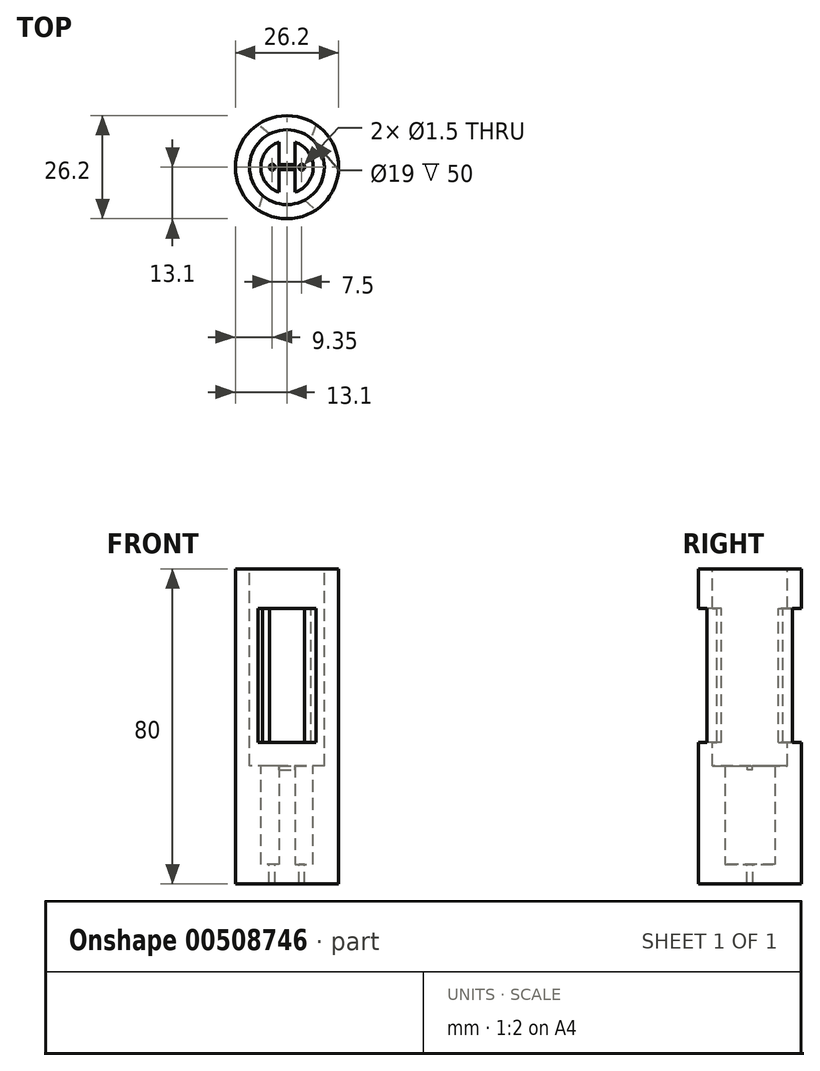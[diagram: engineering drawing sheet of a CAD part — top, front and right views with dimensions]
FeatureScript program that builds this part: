
annotation { "Feature Type Name" : "Feature", "Feature Type Description" : "" }
export const myFeature = defineFeature(function(context is Context, id is Id, definition is map)
    precondition{}
    {
        {
            var Q0;
            Q0=qCreatedBy(makeId("Top.planeOp"),FACE);
            var sketch = newSketch(context, id + "F0", { "sketchPlane" : qUnion([Q0])});
            skCircle(sketch, "E0", {"center": v(0, 0) * mm, "radius": 13.1 * mm});
            skSolve(sketch);
        }
        {
            var Q0;
            Q0=makeQuery(id+"F0.imprint","IMPRINT",FACE,{"disambiguationData":[TD([[makeQuery(id+"F0.imprint","IMPRINT",EDGE,{"derivedFrom":sQuery(id+"F0.wireOp",EDGE,"E0")}),1.0]])]});
            extrude(context, id + "F1", {"entities" : qUnion([Q0]), "depth" : 80 * mm, "offsetDistance" : 25 * mm});
        }
        {
            var Q0;
            Q0=makeQuery(id+"F1.opExtrude","CAP_FACE",FACE,{"disambiguationData":[OSD([sQuery(id+"F0.wireOp",EDGE,"E0")])],"isStart":false});
            var sketch = newSketch(context, id + "F2", { "sketchPlane" : qUnion([Q0])});
            skCircle(sketch, "E1", {"center": v(0, 0) * mm, "radius": 9.5 * mm});
            skSolve(sketch);
        }
        {
            var Q0;
            Q0=makeQuery(id+"F2.imprint","IMPRINT",FACE,{"disambiguationData":[TD([[makeQuery(id+"F2.imprint","IMPRINT",EDGE,{"derivedFrom":sQuery(id+"F2.wireOp",EDGE,"E1")}),1.0]])]});
            var Q1;
            Q1=sQuery(id+"F2.wireOp",EDGE,"E1");
            extrude(context, id + "F3", {"entities" : qUnion([Q0]), "operationType" : NewBodyOperationType.REMOVE, "surfaceEntities" : qUnion([Q1]), "oppositeDirection" : true, "depth" : 50 * mm, "offsetDistance" : 25 * mm});
        }
        {
            var Q0;
            Q0=makeQuery(id+"F3.boolean.opBoolean","COPY",FACE,{"derivedFrom":makeQuery(id+"F3.opExtrude","CAP_FACE",FACE,{"disambiguationData":[OSD([sQuery(id+"F2.wireOp",EDGE,"E1")])],"isStart":false})});
            var sketch = newSketch(context, id + "F4", { "sketchPlane" : qUnion([Q0])});
            skCircle(sketch, "E2", {"center": v(0, 0) * mm, "radius": 6.65 * mm});
            skSolve(sketch);
        }
        {
            var Q0;
            Q0 = qSketchRegion(id + "F4", true);
            extrude(context, id + "F5", {"entities" : qUnion([Q0]), "operationType" : NewBodyOperationType.REMOVE, "oppositeDirection" : true, "depth" : 25 * mm, "offsetDistance" : 25 * mm});
        }
        {
            var Q0;
            Q0=makeQuery(id+"F5.boolean.opBoolean","COPY",FACE,{"derivedFrom":makeQuery(id+"F5.opExtrude","CAP_FACE",FACE,{"disambiguationData":[OSD([sQuery(id+"F4.wireOp",EDGE,"E2")])],"isStart":false})});
            var sketch = newSketch(context, id + "F6", { "sketchPlane" : qUnion([Q0])});
            skLineSegment(sketch, "E3", {"start": v(-2, 6.34) * mm, "end": v(-2, -6.34) * mm});
            skLineSegment(sketch, "E4", {"start": v(2, -6.34) * mm, "end": v(2, 6.34) * mm});
            skSolve(sketch);
        }
        {
            var Q0;
            {var subQ0=sQuery(id+"F6.wireOp",EDGE,"E3");Q0=makeQuery(id+"F6.imprint","IMPRINT",FACE,{"disambiguationData":[TD([[makeQuery(id+"F6.imprint","IMPRINT",EDGE,{"derivedFrom":subQ0}),1.0]])]});}
            extrude(context, id + "F7", {"entities" : qUnion([Q0]), "operationType" : NewBodyOperationType.ADD, "depth" : 25 * mm, "offsetDistance" : 25 * mm});
        }
        {
            var Q0;
            {var subQ0=sQuery(id+"F4.wireOp",EDGE,"E2");Q0=makeQuery(id+"F7.boolean.opBoolean","SPLIT",FACE,{"disambiguationData":[TD([makeQuery(id+"F7.opExtrude","SWEPT_FACE",FACE,{"disambiguationData":[OSD([sQuery(id+"F6.wireOp",EDGE,"E3")])]})])],"derivedFrom":makeQuery(id+"F5.boolean.opBoolean","COPY",FACE,{"derivedFrom":makeQuery(id+"F5.opExtrude","CAP_FACE",FACE,{"disambiguationData":[OSD([subQ0])],"isStart":false})})});}
            var sketch = newSketch(context, id + "F8", { "sketchPlane" : qUnion([Q0])});
            skCircle(sketch, "E5", {"center": v(-3.75, 0) * mm, "radius": 0.75 * mm});
            skCircle(sketch, "E6", {"center": v(3.75, 0) * mm, "radius": 0.75 * mm});
            skSolve(sketch);
        }
        {
            var Q0;
            Q0 = qSketchRegion(id + "F8", true);
            extrude(context, id + "F9", {"entities" : qUnion([Q0]), "operationType" : NewBodyOperationType.REMOVE, "oppositeDirection" : true, "depth" : 5 * mm, "offsetDistance" : 25 * mm});
        }
        {
            var Q0;
            Q0=makeQuery(id+"F7.opExtrude","CAP_FACE",FACE,{"disambiguationData":[OSD([sQuery(id+"F4.wireOp",EDGE,"E2"),sQuery(id+"F6.wireOp",EDGE,"E3"),sQuery(id+"F6.wireOp",EDGE,"E4")])],"isStart":false});
            var sketch = newSketch(context, id + "F10", { "sketchPlane" : qUnion([Q0])});
            skLineSegment(sketch, "E7", {"start": v(-2, 0.6) * mm, "end": v(2, 0.6) * mm});
            skLineSegment(sketch, "E8", {"start": v(-2, -0.6) * mm, "end": v(2, -0.6) * mm});
            skSolve(sketch);
        }
        {
            var Q0;
            {var subQ0=sQuery(id+"F10.wireOp",EDGE,"E7");Q0=makeQuery(id+"F10.imprint","IMPRINT",FACE,{"disambiguationData":[TD([[makeQuery(id+"F10.imprint","IMPRINT",EDGE,{"derivedFrom":subQ0}),-1.0]])]});}
            extrude(context, id + "F11", {"entities" : qUnion([Q0]), "operationType" : NewBodyOperationType.REMOVE, "oppositeDirection" : true, "depth" : 1 * mm, "offsetDistance" : 25 * mm});
        }
        {
            var Q0;
            Q0=makeQuery(id+"F1.opExtrude","CAP_FACE",FACE,{"disambiguationData":[OSD([sQuery(id+"F0.wireOp",EDGE,"E0")])],"isStart":false});
            var sketch = newSketch(context, id + "F12", { "sketchPlane" : qUnion([Q0])});
            skLineSegment(sketch, "E9", {"start": v(-4.43, 8.4) * mm, "end": v(-7.34, 10.85) * mm});
            skLineSegment(sketch, "E10", {"start": v(7.34, 10.85) * mm, "end": v(6.15, 7.24) * mm});
            skLineSegment(sketch, "E11", {"start": v(4.43, -8.4) * mm, "end": v(7.34, -10.85) * mm});
            skLineSegment(sketch, "E12", {"start": v(-6.15, -7.24) * mm, "end": v(-7.34, -10.85) * mm});
            skSolve(sketch);
        }
        {
            var Q0;
            {var subQ0=sQuery(id+"F12.wireOp",EDGE,"E9");Q0=makeQuery(id+"F12.imprint","IMPRINT",FACE,{"disambiguationData":[TD([[makeQuery(id+"F12.imprint","IMPRINT",EDGE,{"derivedFrom":subQ0}),-1.0]])]});}
            extrude(context, id + "F13", {"entities" : qUnion([Q0]), "operationType" : NewBodyOperationType.REMOVE, "oppositeDirection" : true, "depth" : 44 * mm, "offsetDistance" : 25 * mm});
        }
        {
            var Q0;
            {var subQ0=sQuery(id+"F12.wireOp",EDGE,"E11");Q0=makeQuery(id+"F12.imprint","IMPRINT",FACE,{"disambiguationData":[TD([[makeQuery(id+"F12.imprint","IMPRINT",EDGE,{"derivedFrom":subQ0}),-1.0]])]});}
            extrude(context, id + "F14", {"entities" : qUnion([Q0]), "operationType" : NewBodyOperationType.REMOVE, "oppositeDirection" : true, "depth" : 44 * mm});
        }
        {
            var Q0;
            {var subQ0=sQuery(id+"F12.wireOp",EDGE,"E11");Q0=makeQuery(id+"F12.imprint","IMPRINT",FACE,{"disambiguationData":[TD([[makeQuery(id+"F12.imprint","IMPRINT",EDGE,{"derivedFrom":subQ0}),-1.0]])]});}
            extrude(context, id + "F15", {"entities" : qUnion([Q0]), "operationType" : NewBodyOperationType.ADD, "oppositeDirection" : true, "depth" : 10 * mm});
        }
        {
            var Q0;
            {var subQ0=sQuery(id+"F12.wireOp",EDGE,"E9");Q0=makeQuery(id+"F12.imprint","IMPRINT",FACE,{"disambiguationData":[TD([[makeQuery(id+"F12.imprint","IMPRINT",EDGE,{"derivedFrom":subQ0}),-1.0]])]});}
            extrude(context, id + "F16", {"entities" : qUnion([Q0]), "operationType" : NewBodyOperationType.ADD, "oppositeDirection" : true, "depth" : 10 * mm});
        }
    });
